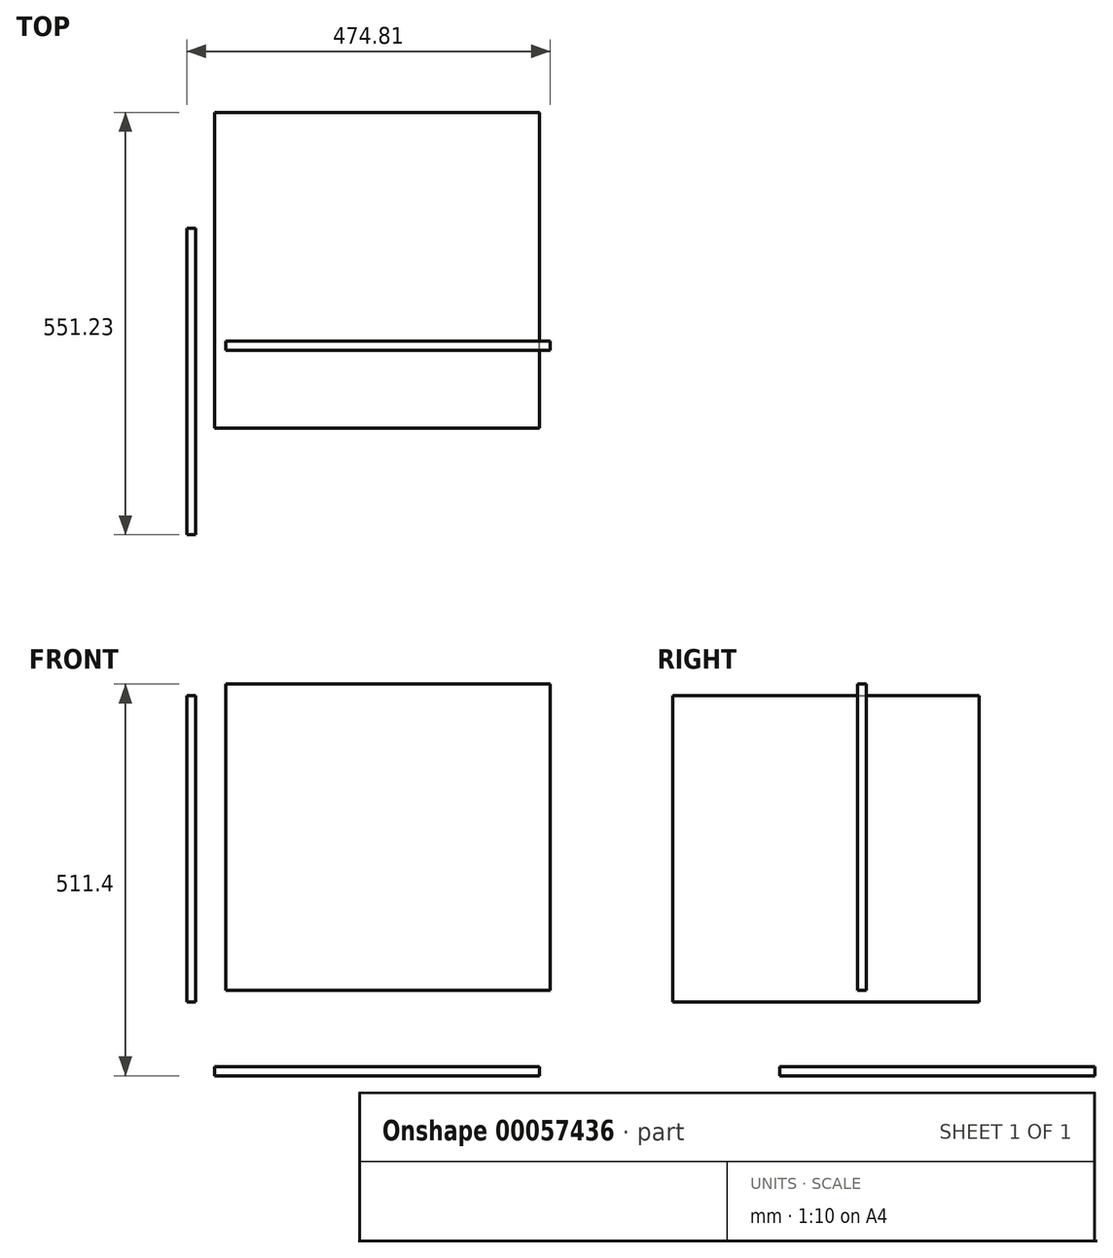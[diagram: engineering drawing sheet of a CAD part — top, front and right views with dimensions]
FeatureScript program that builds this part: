
annotation { "Feature Type Name" : "Feature", "Feature Type Description" : "" }
export const myFeature = defineFeature(function(context is Context, id is Id, definition is map)
    precondition{}
    {
        {
            var Q0;
            Q0=qCreatedBy(makeId("Front.planeOp"),FACE);
            var sketch = newSketch(context, id + "F0", { "sketchPlane" : qUnion([Q0])});
            skLineSegment(sketch, "E0.bottom", {"start": v(-99.2, -88.6) * mm, "end": v(324.8, -88.6) * mm});
            skLineSegment(sketch, "E0.top", {"start": v(-99.2, 311.4) * mm, "end": v(324.8, 311.4) * mm});
            skLineSegment(sketch, "E0.left", {"start": v(-99.2, -88.6) * mm, "end": v(-99.2, 311.4) * mm});
            skLineSegment(sketch, "E0.right", {"start": v(324.8, -88.6) * mm, "end": v(324.8, 311.4) * mm});
            skSolve(sketch);
        }
        {
            var Q0;
            Q0 = qSketchRegion(id + "F0", true);
            extrude(context, id + "F1", {"entities" : qUnion([Q0]), "depth" : 12 * mm});
        }
        {
            var Q0;
            Q0=qCreatedBy(makeId("Top.planeOp"),FACE);
            cPlane(context, id + "F2", {"entities" : qUnion([Q0]), "cplaneType" : CPlaneType.OFFSET, "offset" : 200 * mm, "oppositeDirection" : true, "width" : 150 * mm, "height" : 150 * mm});
        }
        {
            var Q0;
            Q0=qCreatedBy(id+"F2.planeOp",FACE);
            var sketch = newSketch(context, id + "F3", { "sketchPlane" : qUnion([Q0])});
            skLineSegment(sketch, "E1.bottom", {"start": v(-113.65, -113.61) * mm, "end": v(310.35, -113.61) * mm});
            skLineSegment(sketch, "E1.top", {"start": v(-113.65, 298.39) * mm, "end": v(310.35, 298.39) * mm});
            skLineSegment(sketch, "E1.left", {"start": v(-113.65, -113.61) * mm, "end": v(-113.65, 298.39) * mm});
            skLineSegment(sketch, "E1.right", {"start": v(310.35, -113.61) * mm, "end": v(310.35, 298.39) * mm});
            skSolve(sketch);
        }
        {
            var Q0;
            Q0 = qSketchRegion(id + "F3", true);
            extrude(context, id + "F4", {"entities" : qUnion([Q0]), "operationType" : NewBodyOperationType.ADD, "depth" : 12 * mm});
        }
        {
            var Q0;
            Q0=qCreatedBy(makeId("Right.planeOp"),FACE);
            cPlane(context, id + "F5", {"entities" : qUnion([Q0]), "cplaneType" : CPlaneType.OFFSET, "offset" : 150 * mm, "oppositeDirection" : true, "width" : 150 * mm, "height" : 150 * mm});
        }
        {
            var Q0;
            Q0=qCreatedBy(id+"F5.planeOp",FACE);
            var sketch = newSketch(context, id + "F6", { "sketchPlane" : qUnion([Q0])});
            skLineSegment(sketch, "E2.bottom", {"start": v(-252.84, -103.48) * mm, "end": v(147.16, -103.48) * mm});
            skLineSegment(sketch, "E2.top", {"start": v(-252.84, 296.52) * mm, "end": v(147.16, 296.52) * mm});
            skLineSegment(sketch, "E2.left", {"start": v(-252.84, -103.48) * mm, "end": v(-252.84, 296.52) * mm});
            skLineSegment(sketch, "E2.right", {"start": v(147.16, -103.48) * mm, "end": v(147.16, 296.52) * mm});
            skSolve(sketch);
        }
        {
            var Q0;
            Q0=makeQuery(id+"F6.imprint","IMPRINT",FACE,{"disambiguationData":[TD([[makeQuery(id+"F6.imprint","IMPRINT",EDGE,{"derivedFrom":sQuery(id+"F6.wireOp",EDGE,"E2.bottom")}),1.0]])]});
            extrude(context, id + "F7", {"entities" : qUnion([Q0]), "depth" : 12 * mm});
        }
    });
